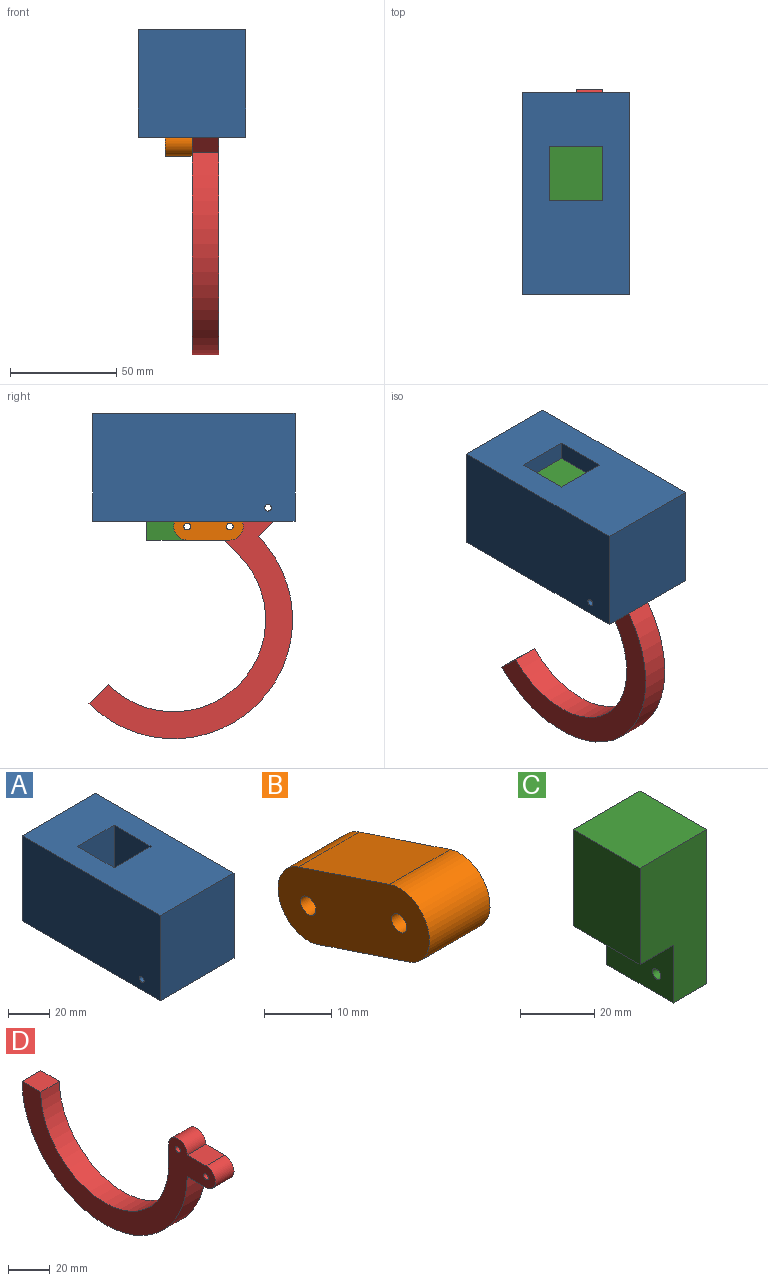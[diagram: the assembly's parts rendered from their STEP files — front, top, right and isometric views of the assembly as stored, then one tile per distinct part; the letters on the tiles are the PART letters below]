
ASSEMBLY  parts=4 mates=3
PART A: 17 faces, bbox 50.8x95.3x50.8 mm
  f0: plane 12.7x12.7mm, normal (0,1,0), area 161.3mm2, adj f3,f4,f12,f14
  f1: plane 50.8x44.45mm, normal (1,0,0), area 1653.2mm2, adj f3,f5,f6,f7,f8,f9
  f2: plane 50.8x50.8mm, normal (0,-1,0), area 2580.6mm2, adj f3,f8,f11,f13
  f3: plane 95.25x50.8mm, normal (0,0,-1), area 3467.7mm2, adj f0,f1,f2,f5,f9,f10,f11,f12
  f4: plane 19.05x12.7mm, normal (0,0,-1), area 241.9mm2, adj f0,f5,f12,f14
  f5: plane 25.4x19.05mm, normal (0,1,0), area 322.6mm2, adj f1,f3,f4,f6,f12,f14
  f6: plane 25.4x19.05mm, normal (0,0,-1), area 483.9mm2, adj f1,f5,f7,f12
  f7: plane 31.75x25.4mm, normal (0,1,0), area 806.5mm2, adj f1,f6,f8,f12
  f8: plane 95.25x50.8mm, normal (0,0,1), area 4193.5mm2, adj f1,f2,f7,f9,f10,f11,f12,f13
  f9: plane 50.8x25.4mm, normal (0,-1,0), area 1290.3mm2, adj f1,f3,f8,f12
  f10: plane 50.8x50.8mm, normal (0,1,0), area 2580.6mm2, adj f3,f8,f11,f13
  f11: plane 95.25x50.8mm, normal (1,0,0), area 4830.8mm2, adj f2,f3,f8,f10,f16
  f12: plane 63.5x50.8mm, normal (-1,0,0), area 1887.2mm2, adj f0,f3,f4,f5,f6,f7,f8,f9
  f13: plane 95.25x50.8mm, normal (-1,0,0), area 4830.8mm2, adj f2,f3,f8,f10,f15
  f14: plane 19.05x12.7mm, normal (1,0,0), area 234mm2, adj f0,f3,f4,f5,f15
  f15: cylinder r=1.59mm len=25.4mm, axis (1,0,0), area 253.4mm2, adj f13,f14
  f16: cylinder r=1.59mm len=12.7mm, axis (1,0,0), area 126.7mm2, adj f11,f12
PART B: 8 faces, bbox 12.7x31.8x19.1 mm
  f0: cylinder r=6.35mm len=12.7mm, axis (1,0,0), area 253.4mm2, adj f1,f3,f6,f7
  f1: plane 19.05x12.7mm, normal (0,-0.32,-0.95), area 255mm2, adj f0,f2,f6,f7
  f2: cylinder r=6.35mm len=12.7mm, axis (1,0,0), area 253.4mm2, adj f1,f3,f6,f7
  f3: plane 19.05x12.7mm, normal (0,0.32,0.95), area 255mm2, adj f0,f2,f6,f7
  f4: cylinder r=1.59mm len=12.7mm, axis (1,0,0), area 126.7mm2, adj f6,f7
  f5: cylinder r=1.59mm len=12.7mm, axis (1,0,0), area 126.7mm2, adj f6,f7
  f6: plane 31.75x19.05mm, normal (-1,0,0), area 365.9mm2, adj f0,f1,f2,f3,f4,f5
  f7: plane 31.75x19.05mm, normal (1,0,0), area 365.9mm2, adj f0,f1,f2,f3,f4,f5
PART C: 9 faces, bbox 25.4x25.4x50.8 mm
  f0: plane 50.8x25.4mm, normal (0,-1,0), area 1048.4mm2, adj f1,f3,f5,f6,f7,f8
  f1: plane 25.4x12.7mm, normal (0,0,-1), area 322.6mm2, adj f0,f2,f5,f6
  f2: plane 50.8x25.4mm, normal (0,1,0), area 1048.4mm2, adj f1,f3,f5,f6,f7,f8
  f3: plane 25.4x25.4mm, normal (0,0,1), area 645.2mm2, adj f0,f2,f5,f8
  f4: cylinder r=1.59mm len=12.7mm, axis (-1,0,0), area 126.7mm2, adj f5,f6
  f5: plane 50.8x25.4mm, normal (1,0,0), area 1282.4mm2, adj f0,f1,f2,f3,f4
  f6: plane 25.4x19.05mm, normal (-1,0,0), area 476mm2, adj f0,f1,f2,f4,f7
  f7: plane 25.4x12.7mm, normal (0,0,-1), area 322.6mm2, adj f0,f2,f6,f8
  f8: plane 31.75x25.4mm, normal (-1,0,0), area 806.4mm2, adj f0,f2,f3,f7
PART D: 12 faces, bbox 12.7x131.1x75.1 mm
  f0: cylinder r=6.35mm len=12.7mm, axis (-1,0,0), area 253.4mm2, adj f1,f4,f7,f8
  f1: plane 12.7x12.7mm, normal (0,0,1), area 161.3mm2, adj f0,f2,f7,f8
  f2: cylinder r=6.35mm len=12.7mm, axis (-1,0,0), area 253.4mm2, adj f1,f3,f7,f8
  f3: plane 12.7x12.7mm, normal (0,0,-1), area 161.3mm2, adj f2,f7,f8,f10
  f4: plane 12.7x12.7mm, normal (0,1,0), area 161.3mm2, adj f0,f7,f8,f9
  f5: cylinder r=1.59mm len=12.7mm, axis (-1,0,0), area 126.7mm2, adj f7,f8
  f6: cylinder r=1.59mm len=12.7mm, axis (-1,0,0), area 126.7mm2, adj f7,f8
  f7: plane 131.15x75.1mm, normal (1,0,0), area 2416.3mm2, adj f0,f1,f2,f3,f4,f5,f6,f9
  f8: plane 131.15x75.1mm, normal (-1,0,0), area 2416.3mm2, adj f0,f1,f2,f3,f4,f5,f6,f9
  f9: cylinder r=43.35mm len=86.7mm, axis (1,0,0), area 1729.5mm2, adj f4,f7,f8,f11
  f10: cylinder r=56.05mm len=112.1mm, axis (1,0,0), area 2236.2mm2, adj f3,f7,f8,f11
  f11: plane 12.7x12.7mm, normal (0,0,1), area 161.3mm2, adj f7,f8,f9,f10
PLACE A rot(axis=(1,0,0),0deg) t=(0,31.75,-12.7)mm
PLACE B rot(axis=(1,0,0),18.4deg) t=(0,30.72,-27.91)mm
PLACE C rot(axis=(-0.06,0.06,-1),0deg) t=(0,31.75,-21.56)mm
PLACE D rot(axis=(-1,0,0),44.6deg) t=(0,30.72,-27.91)mm
MATE revolute C.f4 <-> B.f0  axis (-1,0,0) through (0,50.8,-27.91)mm
MATE revolute D.f5 <-> B.f5  axis (-1,0,0) through (0,30.72,-27.91)mm
MATE revolute D.f2 <-> A.f15  axis (-1,0,0) through (0,12.7,-19.05)mm
